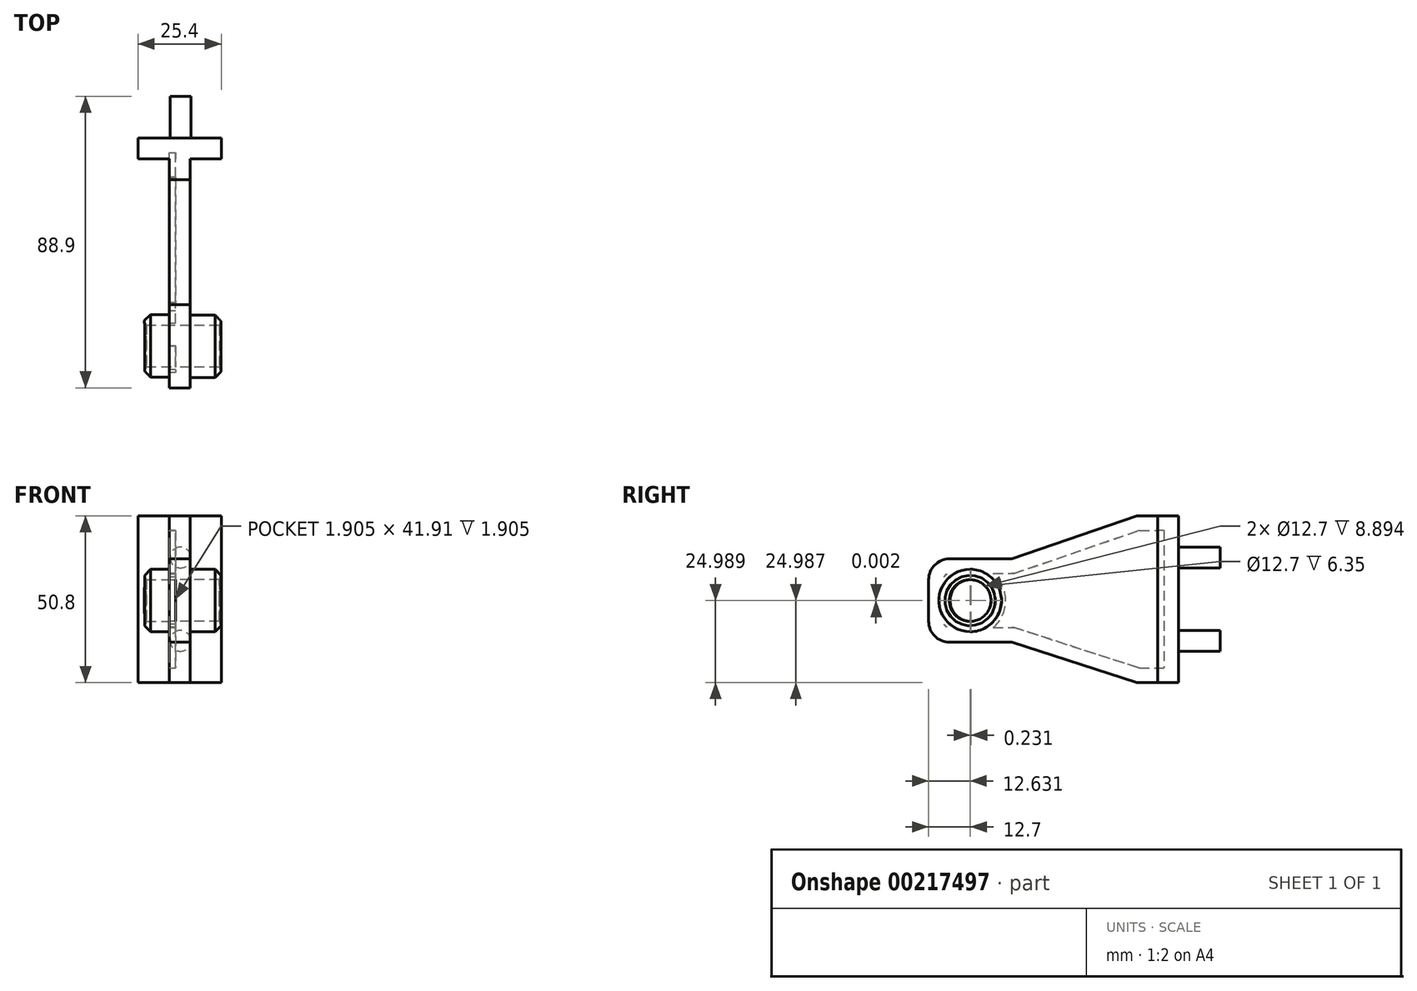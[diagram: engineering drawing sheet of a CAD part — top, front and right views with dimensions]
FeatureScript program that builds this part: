
annotation { "Feature Type Name" : "Feature", "Feature Type Description" : "" }
export const myFeature = defineFeature(function(context is Context, id is Id, definition is map)
    precondition{}
    {
        {
            var Q0;
            Q0=qCreatedBy(makeId("Front.planeOp"),FACE);
            var sketch = newSketch(context, id + "F0", { "sketchPlane" : qUnion([Q0])});
            skLineSegment(sketch, "E0.bottom", {"start": v(0, 0) * mm, "end": v(25.4, 0) * mm});
            skLineSegment(sketch, "E0.top", {"start": v(0, 50.8) * mm, "end": v(25.4, 50.8) * mm});
            skLineSegment(sketch, "E0.left", {"start": v(0, 0) * mm, "end": v(0, 50.8) * mm});
            skLineSegment(sketch, "E0.right", {"start": v(25.4, 0) * mm, "end": v(25.4, 50.8) * mm});
            skSolve(sketch);
        }
        {
            var Q0;
            Q0 = qSketchRegion(id + "F0", true);
            extrude(context, id + "F1", {"entities" : qUnion([Q0]), "depth" : 6.35 * mm});
        }
        {
            var Q0;
            Q0=qCreatedBy(makeId("Front.planeOp"),FACE);
            var sketch = newSketch(context, id + "F2", { "sketchPlane" : qUnion([Q0])});
            skLineSegment(sketch, "E1.bottom", {"start": v(9.53, 0) * mm, "end": v(15.87, 0) * mm});
            skLineSegment(sketch, "E1.top", {"start": v(9.52, 50.8) * mm, "end": v(15.87, 50.8) * mm});
            skLineSegment(sketch, "E1.left", {"start": v(9.53, 0) * mm, "end": v(9.52, 50.8) * mm});
            skLineSegment(sketch, "E1.right", {"start": v(15.87, 0) * mm, "end": v(15.87, 50.8) * mm});
            skSolve(sketch);
        }
        {
            var Q0;
            Q0 = qSketchRegion(id + "F2", true);
            extrude(context, id + "F3", {"entities" : qUnion([Q0]), "operationType" : NewBodyOperationType.ADD, "depth" : 12.7 * mm});
        }
        {
            var Q0;
            Q0=qCreatedBy(makeId("Front.planeOp"),FACE);
            cPlane(context, id + "F4", {"entities" : qUnion([Q0]), "cplaneType" : CPlaneType.OFFSET, "offset" : 50.8 * mm, "width" : 152.4 * mm, "height" : 152.4 * mm});
        }
        {
            var Q0;
            Q0=qCreatedBy(id+"F4.planeOp",FACE);
            var sketch = newSketch(context, id + "F5", { "sketchPlane" : qUnion([Q0])});
            skLineSegment(sketch, "E2.bottom", {"start": v(9.54, 37.69) * mm, "end": v(15.89, 37.69) * mm});
            skLineSegment(sketch, "E2.top", {"start": v(9.54, 12.29) * mm, "end": v(15.89, 12.29) * mm});
            skLineSegment(sketch, "E2.left", {"start": v(9.54, 37.69) * mm, "end": v(9.54, 12.29) * mm});
            skLineSegment(sketch, "E2.right", {"start": v(15.89, 37.69) * mm, "end": v(15.89, 12.29) * mm});
            skSolve(sketch);
        }
        {
            var Q1;
            Q1=makeQuery(id+"F3.opExtrude","CAP_FACE",FACE,{"disambiguationData":[OSD([sQuery(id+"F2.wireOp",EDGE,"E1.bottom"),sQuery(id+"F2.wireOp",EDGE,"E1.top"),sQuery(id+"F2.wireOp",EDGE,"E1.left"),sQuery(id+"F2.wireOp",EDGE,"E1.right")])],"isStart":false});
            var Q2;
            Q2=makeQuery(id+"F5.imprint","IMPRINT",FACE,{"disambiguationData":[TD([[makeQuery(id+"F5.imprint","IMPRINT",EDGE,{"derivedFrom":sQuery(id+"F5.wireOp",EDGE,"E2.bottom")}),-1.0]])]});
            loft(context, id + "F6", {"operationType" : NewBodyOperationType.ADD, "sheetProfilesArray" : [{ "sheetProfileEntities" : qUnion([Q1]) }, { "sheetProfileEntities" : qUnion([Q2]) }]});
        }
        {
            var Q0;
            Q0=makeQuery(id+"F6.opLoft","CAP_FACE",FACE,{"disambiguationData":[OSD([makeQuery(id+"F5.imprint","IMPRINT",FACE,{"disambiguationData":[TD([[makeQuery(id+"F5.imprint","IMPRINT",EDGE,{"derivedFrom":sQuery(id+"F5.wireOp",EDGE,"E2.bottom")}),-1.0]])]})])],"isStart":true});
            extrude(context, id + "F7", {"entities" : qUnion([Q0]), "operationType" : NewBodyOperationType.ADD, "depth" : 25.4 * mm});
        }
        {
            var Q0;
            Q0=makeQuery(id+"F7.opExtrude","CAP_EDGE",EDGE,{"disambiguationData":[OSD([sQuery(id+"F5.wireOp",EDGE,"E2.bottom"),sQuery(id+"F5.wireOp",EDGE,"E2.left"),sQuery(id+"F5.wireOp",EDGE,"E2.right")])],"isStart":false});
            var Q1;
            Q1=makeQuery(id+"F7.opExtrude","CAP_EDGE",EDGE,{"disambiguationData":[OSD([sQuery(id+"F5.wireOp",EDGE,"E2.top"),sQuery(id+"F5.wireOp",EDGE,"E2.left"),sQuery(id+"F5.wireOp",EDGE,"E2.right")])],"isStart":false});
            fillet(context, id + "F8", {"entities" : qUnion([Q0, Q1]), "radius" : 6.35 * mm, "tangentPropagation" : true, "allowEdgeOverflow" : false});
        }
        {
            var Q0;
            Q0=makeQuery(id+"F7.opExtrude","SWEPT_FACE",FACE,{"disambiguationData":[OSD([sQuery(id+"F5.wireOp",EDGE,"E2.bottom"),sQuery(id+"F5.wireOp",EDGE,"E2.top"),sQuery(id+"F5.wireOp",EDGE,"E2.left")])]});
            var sketch = newSketch(context, id + "F9", { "sketchPlane" : qUnion([Q0])});
            skPoint(sketch, "E3", {"position": v(63.5, 24.99) * mm});
            skPoint(sketch, "E3.positionSnap0", {"position": v(76.2, 24.99) * mm});
            skSolve(sketch);
        }
        {
            var Q0;
            Q0=sQuery(id+"F9.wireOp",VERTEX,"E3");
            var Q1;
            Q1=makeQuery(id+"F1.opExtrude","SWEPT_BODY",BODY,{"disambiguationData":[OSD([sQuery(id+"F0.wireOp",EDGE,"E0.bottom"),sQuery(id+"F0.wireOp",EDGE,"E0.top"),sQuery(id+"F0.wireOp",EDGE,"E0.left"),sQuery(id+"F0.wireOp",EDGE,"E0.right")])]});
            hole(context, id + "F10", {"style" : HoleStyle.SIMPLE, "endStyle" : HoleEndStyle.THROUGH, "holeDiameter" : 12.7 * mm, "locations" : qUnion([Q0]), "scope" : qUnion([Q1]), "isTappedThrough" : true});
        }
        {
            var Q0;
            Q0=qCreatedBy(makeId("Front.planeOp"),FACE);
            var sketch = newSketch(context, id + "F11", { "sketchPlane" : qUnion([Q0])});
            skCircle(sketch, "E4", {"center": v(12.93, 12.7) * mm, "radius": 3.18 * mm});
            skCircle(sketch, "E5", {"center": v(12.96, 38.1) * mm, "radius": 3.18 * mm});
            skSolve(sketch);
        }
        {
            var Q0;
            Q0 = qSketchRegion(id + "F11", true);
            extrude(context, id + "F12", {"entities" : qUnion([Q0]), "operationType" : NewBodyOperationType.ADD, "oppositeDirection" : true, "depth" : 12.7 * mm});
        }
        {
            var Q0;
            Q0=makeQuery(id+"F6.opLoft","SWEPT_FACE",FACE,{"disambiguationData":[OSD([sQuery(id+"F2.wireOp",EDGE,"E1.bottom"),sQuery(id+"F2.wireOp",EDGE,"E1.top"),sQuery(id+"F2.wireOp",EDGE,"E1.left"),sQuery(id+"F5.wireOp",EDGE,"E2.bottom"),sQuery(id+"F5.wireOp",EDGE,"E2.top"),sQuery(id+"F5.wireOp",EDGE,"E2.left")])]});
            var Q1;
            Q1=makeQuery(id+"F3.opExtrude","SWEPT_FACE",FACE,{"disambiguationData":[OSD([sQuery(id+"F2.wireOp",EDGE,"E1.left")])]});
            var Q2;
            Q2=makeQuery(id+"F7.opExtrude","SWEPT_FACE",FACE,{"disambiguationData":[OSD([sQuery(id+"F5.wireOp",EDGE,"E2.bottom"),sQuery(id+"F5.wireOp",EDGE,"E2.top"),sQuery(id+"F5.wireOp",EDGE,"E2.left")])]});
            shell(context, id + "F13", {"entities" : qUnion([Q0, Q1, Q2]), "thickness" : 4.44 * mm});
        }
        {
            var Q0;
            Q0=makeQuery(id+"F6.opLoft","SWEPT_FACE",FACE,{"disambiguationData":[OSD([sQuery(id+"F2.wireOp",EDGE,"E1.bottom"),sQuery(id+"F2.wireOp",EDGE,"E1.top"),sQuery(id+"F2.wireOp",EDGE,"E1.right"),sQuery(id+"F5.wireOp",EDGE,"E2.bottom"),sQuery(id+"F5.wireOp",EDGE,"E2.top"),sQuery(id+"F5.wireOp",EDGE,"E2.right")])]});
            var sketch = newSketch(context, id + "F14", { "sketchPlane" : qUnion([Q0])});
            skCircle(sketch, "E6", {"center": v(-63.58, 24.99) * mm, "radius": 9.53 * mm});
            skCircle(sketch, "E7", {"center": v(-63.58, 24.99) * mm, "radius": 6.35 * mm});
            skSolve(sketch);
        }
        {
            var Q0;
            Q0=makeQuery(id+"F14.imprint","IMPRINT",FACE,{"disambiguationData":[TD([[makeQuery(id+"F14.imprint","IMPRINT",EDGE,{"derivedFrom":sQuery(id+"F14.wireOp",EDGE,"E6")}),1.0]])]});
            extrude(context, id + "F15", {"entities" : qUnion([Q0]), "depth" : 12.7 * mm});
        }
        {
            var Q0;
            Q0=makeQuery(id+"F13.opShell","OFFSET_FACE",FACE,{"disambiguationData":[OSD([sQuery(id+"F2.wireOp",EDGE,"E1.bottom"),sQuery(id+"F2.wireOp",EDGE,"E1.top"),sQuery(id+"F2.wireOp",EDGE,"E1.right"),sQuery(id+"F5.wireOp",EDGE,"E2.bottom"),sQuery(id+"F5.wireOp",EDGE,"E2.top"),sQuery(id+"F5.wireOp",EDGE,"E2.right")])]});
            var sketch = newSketch(context, id + "F16", { "sketchPlane" : qUnion([Q0])});
            skCircle(sketch, "E8", {"center": v(63.34, 24.99) * mm, "radius": 9.53 * mm});
            skCircle(sketch, "E9", {"center": v(63.34, 24.99) * mm, "radius": 6.35 * mm});
            skSolve(sketch);
        }
        {
            var Q0;
            Q0 = qSketchRegion(id + "F16", true);
            extrude(context, id + "F17", {"entities" : qUnion([Q0]), "operationType" : NewBodyOperationType.ADD, "depth" : 12.7 * mm});
        }
        {
            var Q0;
            Q0=makeQuery(id+"F15.opExtrude","CAP_EDGE",EDGE,{"disambiguationData":[OSD([sQuery(id+"F14.wireOp",EDGE,"E6")])],"isStart":false});
            var Q1;
            Q1=makeQuery(id+"F17.opExtrude","CAP_EDGE",EDGE,{"disambiguationData":[OSD([sQuery(id+"F16.wireOp",EDGE,"E8")])],"isStart":false});
            chamfer(context, id + "F18", {"entities" : qUnion([Q0, Q1]), "width" : 5.08 * mm, "tangentPropagation" : true});
        }
        {
            var Q0;
            Q0=makeQuery(id+"F18.opChamfer","BLEND_EDGE",EDGE,{"blendedFrom":[makeQuery(id+"F15.opExtrude","CAP_EDGE",EDGE,{"disambiguationData":[OSD([sQuery(id+"F14.wireOp",EDGE,"E6")])],"isStart":false}),makeQuery(id+"F15.opExtrude","SWEPT_FACE",FACE,{"disambiguationData":[OSD([sQuery(id+"F14.wireOp",EDGE,"E7")])]})],"blendedInto":[makeQuery(id+"F15.opExtrude","SWEPT_FACE",FACE,{"disambiguationData":[OSD([sQuery(id+"F14.wireOp",EDGE,"E7")])]})]});
            var Q1;
            Q1=makeQuery(id+"F18.opChamfer","BLEND_EDGE",EDGE,{"blendedFrom":[makeQuery(id+"F17.opExtrude","CAP_EDGE",EDGE,{"disambiguationData":[OSD([sQuery(id+"F16.wireOp",EDGE,"E8")])],"isStart":false}),makeQuery(id+"F17.opExtrude","SWEPT_FACE",FACE,{"disambiguationData":[OSD([sQuery(id+"F16.wireOp",EDGE,"E9")])]})],"blendedInto":[makeQuery(id+"F17.opExtrude","SWEPT_FACE",FACE,{"disambiguationData":[OSD([sQuery(id+"F16.wireOp",EDGE,"E9")])]})]});
            chamfer(context, id + "F19", {"entities" : qUnion([Q0, Q1]), "width" : 0.79 * mm, "tangentPropagation" : true});
        }
    });
